# Revit family: Martin Brattrud - Medinah - Sofa - 45 Degree BTB
name_source: partatom
category: Furniture
revit_build: Autodesk Revit LT 2016 (Build: 20151007_0715(x64)
units: mm (PartAtom-declared; Revit-internal decimal feet)

## family parameters
Always vertical = Yes
Cut with Voids When Loaded = No
OmniClass Number = 23.40.20.00
OmniClass Title = General Furniture and Specialties
Room Calculation Point = No
Shared = No
Work Plane-Based = No

## types (3) — shared parameters
ANGLE = 22.50°
Assembly Code = E2020200
DEPTH = 3' - 7"
Description = Medinah, Sofa 45 Degree BTB
Keynote = 125000
Manufacturer = Martin Brattrud, Inc.
SCS Certified Product = Yes
URL = http://www.martinbrattrud.com
WIDTH = 6' - 1"
r = 0' - 0 1/2"

## per-type parameters (varying)
| type | HEIGHT | Model |
| Low Back | 2' - 9" | 1924-80BTB |
| Mid Back | 3' - 7" | 1925-80BTB |
| High Back | 4' - 6" | 1926-80BTB |

## geometry (parser evidence)
native form markers: Sweep x9
no freeform markers — native parametric forms only
